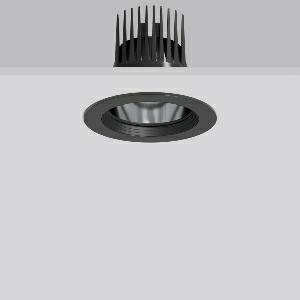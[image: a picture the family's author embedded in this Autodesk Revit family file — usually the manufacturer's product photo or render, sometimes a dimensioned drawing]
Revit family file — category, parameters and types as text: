
# Revit family: heledon_maxi_e_901778_003_cbfe
name_source: partatom
category: Lighting Fixtures
units: mm (PartAtom-declared; Revit-internal decimal feet)

## family parameters
Cut with Voids When Loaded = No
Host = Face
Light Source = No
Part Type = Normal
Room Calculation Point = No
Round Connector Dimension = Use Diameter
Shared = No

## types (1)
- HELEDON maxi E (1 x LED Modul 920 meat+, 2250 lm, 2000)
    Apparent Load = 33 VA
    Approval mark = CE
    CIE Flux Codes = 100 100 100 100 100
    Color Rendering = 90
    Color Temperature = 2000
    Default Elevation = 1800 mm
    Description = Series: HELEDON maxi
Round recessed downlight. Housing: die-cast aluminium, powder-coated. Black plastic ring and recessed LED to prevent glare from the side. Optical assembly with reflector made of MIRO-Silver with 98% total light reflection for outstanding efficiency - can be changed without tools. Special LED for illumination of meat included. Suitable for Recessed ceiling mounting. Installation without tools thanks to spring fastening system. Including separate LED converter with connecting cable 600 mm.High quality converter without flickering and stroboscopic effect. Through-wiring box (5 pole) available as accessory. The following accessories can be mounted without use of tools: interchangeable lenses, decorative glasses, honeycomb louvre, clear and frosted diffusers, white interchangeable plastic ring. 
Colour: deep black, matt (RAL 9005)
Diameter: 162 mm
Height: 3 mm
Cut-out diameter: 152 mm
Recess height: 200 mm
Luminaire: recess height: 135 mm
Lamp: LED
Socket: without socket
Colour temperature: meat +
System power: 33 W
Rated luminous flux: 2250 lm
Luminous efficiency: 68 lm/W
Control gear: Regulated power supply
Protection class: II
Type of protection: IP 20
    Height = 0 mm  [stored 0 ft]
    Lamp = 1 x LED Modul 920 meat+
    Lamp Light Flux = 2250 lm
    Lamp count = 1
    Length = 162 mm
    Lifetime = 50000 h
    Luminous efficacy = 68 lm/W
    Manufacturer = RZB
    ModVariant = No
    Model = 901778.003
    Mounting Place = Ceiling
    Mounting Type = Recessed
    Number of Poles = 1
    OnlyDefault = Yes
    Power Factor = 1
    Product Name = HELEDON maxi E
    Product group = Recessed downlights
    ProductGroupID = 402
    Protection Class = Protection class II
    Protection Degree = IP 20
    RLX_Detail_Level = 1
    RLX_Emergency_Light_Flux = 0 lm
    RLX_Emergency_Type = 0
    RLX_Emergency_Type_DB = No
    RlxData = <blob elided: 122525 chars, md5=bafe1c28>
    Socket = socket
    Standby Power = 0 W
    System Light Flux = 2250 lm
    System Power = 33 W
    Type Comments = Product without accessories
    Type Image = 901662.003.jpg
    URL = http://relux.com
    VarID = ---
    Voltage = 230 V
    Voltage Range = 220-240 V
    Weight = 0.00 kg
    Width = 0 mm  [stored 0 ft]

note: [stored X ft] marks values corroborated as IEEE doubles in the binary element streams (Revit-internal decimal feet)

## geometry (parser evidence)
native form markers: Blend x4, Sweep x11
no freeform markers — native parametric forms only
